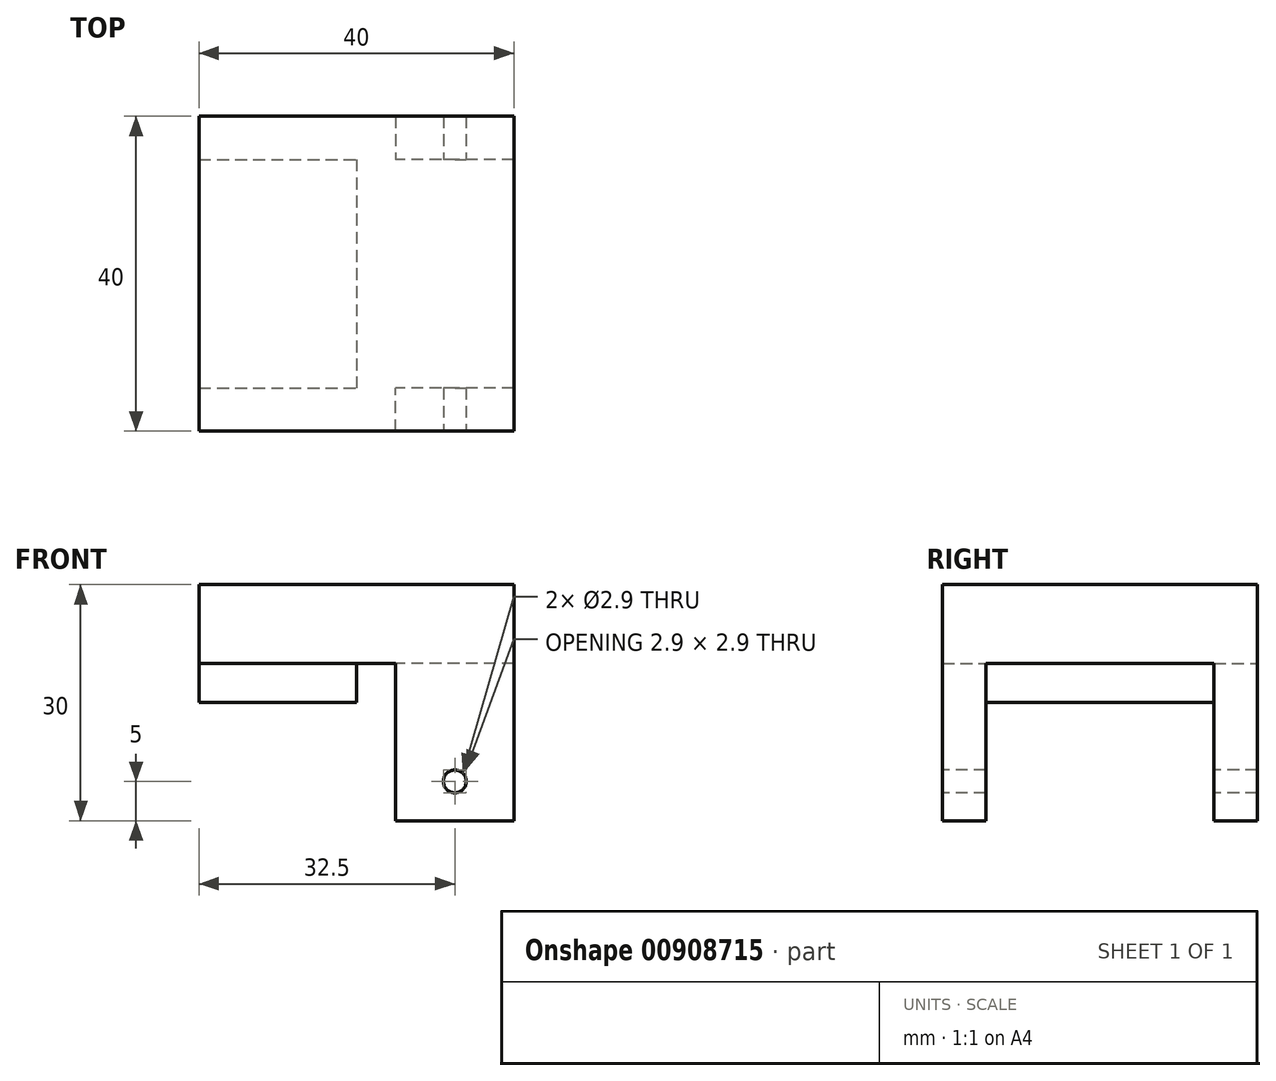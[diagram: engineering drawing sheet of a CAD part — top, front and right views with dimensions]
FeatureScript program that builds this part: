
annotation { "Feature Type Name" : "Feature", "Feature Type Description" : "" }
export const myFeature = defineFeature(function(context is Context, id is Id, definition is map)
    precondition{}
    {
        {
            var Q0;
            Q0=qCreatedBy(makeId("Top.planeOp"),FACE);
            var sketch = newSketch(context, id + "F0", { "sketchPlane" : qUnion([Q0])});
            skLineSegment(sketch, "E0.bottom", {"start": v(20, -20) * mm, "end": v(-20, -20) * mm});
            skLineSegment(sketch, "E0.top", {"start": v(20, 20) * mm, "end": v(-20, 20) * mm});
            skLineSegment(sketch, "E0.left", {"start": v(20, -20) * mm, "end": v(20, 20) * mm});
            skLineSegment(sketch, "E0.right", {"start": v(-20, -20) * mm, "end": v(-20, 20) * mm});
            skPoint(sketch, "E0.middle", {"position": v(0, 0) * mm});
            skSolve(sketch);
        }
        {
            var Q0;
            Q0=makeQuery(id+"F0.imprint","IMPRINT",FACE,{"disambiguationData":[TD([[makeQuery(id+"F0.imprint","IMPRINT",EDGE,{"derivedFrom":sQuery(id+"F0.wireOp",EDGE,"E0.bottom")}),-1.0]])]});
            extrude(context, id + "F1", {"entities" : qUnion([Q0]), "depth" : 10 * mm, "offsetDistance" : 25 * mm});
        }
        {
            var Q0;
            Q0=makeQuery(id+"F1.opExtrude","CAP_FACE",FACE,{"disambiguationData":[OSD([sQuery(id+"F0.wireOp",EDGE,"E0.bottom"),sQuery(id+"F0.wireOp",EDGE,"E0.top"),sQuery(id+"F0.wireOp",EDGE,"E0.left"),sQuery(id+"F0.wireOp",EDGE,"E0.right")])],"isStart":true});
            var sketch = newSketch(context, id + "F2", { "sketchPlane" : qUnion([Q0])});
            skLineSegment(sketch, "E1.bottom", {"start": v(-20, -14.5) * mm, "end": v(0, -14.5) * mm});
            skLineSegment(sketch, "E1.top", {"start": v(-20, 14.5) * mm, "end": v(0, 14.5) * mm});
            skLineSegment(sketch, "E1.left", {"start": v(-20, -14.5) * mm, "end": v(-20, 14.5) * mm});
            skLineSegment(sketch, "E1.right", {"start": v(0, -14.5) * mm, "end": v(0, 14.5) * mm});
            skSolve(sketch);
        }
        {
            var Q0;
            Q0=makeQuery(id+"F2.imprint","IMPRINT",FACE,{"disambiguationData":[TD([[makeQuery(id+"F2.imprint","IMPRINT",EDGE,{"derivedFrom":sQuery(id+"F2.wireOp",EDGE,"E1.bottom")}),1.0]])]});
            extrude(context, id + "F3", {"entities" : qUnion([Q0]), "operationType" : NewBodyOperationType.ADD, "depth" : 5 * mm, "offsetDistance" : 25 * mm});
        }
        {
            var Q0;
            Q0=makeQuery(id+"F1.opExtrude","CAP_FACE",FACE,{"disambiguationData":[OSD([sQuery(id+"F0.wireOp",EDGE,"E0.bottom"),sQuery(id+"F0.wireOp",EDGE,"E0.top"),sQuery(id+"F0.wireOp",EDGE,"E0.left"),sQuery(id+"F0.wireOp",EDGE,"E0.right")])],"isStart":true});
            var sketch = newSketch(context, id + "F4", { "sketchPlane" : qUnion([Q0])});
            skLineSegment(sketch, "E2.bottom", {"start": v(20, 20) * mm, "end": v(5, 20) * mm});
            skLineSegment(sketch, "E2.top", {"start": v(20, 14.5) * mm, "end": v(5, 14.5) * mm});
            skLineSegment(sketch, "E2.left", {"start": v(20, 20) * mm, "end": v(20, 14.5) * mm});
            skLineSegment(sketch, "E2.right", {"start": v(5, 20) * mm, "end": v(5, 14.5) * mm});
            skLineSegment(sketch, "E3.bottom", {"start": v(20, -20) * mm, "end": v(5, -20) * mm});
            skLineSegment(sketch, "E3.top", {"start": v(20, -14.5) * mm, "end": v(5, -14.5) * mm});
            skLineSegment(sketch, "E3.left", {"start": v(20, -20) * mm, "end": v(20, -14.5) * mm});
            skLineSegment(sketch, "E3.right", {"start": v(5, -20) * mm, "end": v(5, -14.5) * mm});
            skSolve(sketch);
        }
        {
            var Q0;
            Q0=makeQuery(id+"F4.imprint","IMPRINT",FACE,{"disambiguationData":[TD([[makeQuery(id+"F4.imprint","IMPRINT",EDGE,{"derivedFrom":sQuery(id+"F4.wireOp",EDGE,"f1VrWO3J-vSY3-jro8-bQ0T-jen6n7x72WjQ.bottom")}),1.0]])]});
            var Q1;
            Q1=makeQuery(id+"F4.imprint","IMPRINT",FACE,{"disambiguationData":[TD([[makeQuery(id+"F4.imprint","IMPRINT",EDGE,{"derivedFrom":sQuery(id+"F4.wireOp",EDGE,"hxVAKMcA-pLjx-TPLh-AbCJ-cGopowbzSFwm.bottom")}),-1.0]])]});
            var Q2;
            Q2=makeQuery(id+"F4.imprint","IMPRINT",FACE,{"disambiguationData":[TD([[makeQuery(id+"F4.imprint","IMPRINT",EDGE,{"derivedFrom":sQuery(id+"F4.wireOp",EDGE,"E2.bottom")}),1.0]])]});
            var Q3;
            Q3=makeQuery(id+"F4.imprint","IMPRINT",FACE,{"disambiguationData":[TD([[makeQuery(id+"F4.imprint","IMPRINT",EDGE,{"derivedFrom":sQuery(id+"F4.wireOp",EDGE,"E3.bottom")}),-1.0]])]});
            extrude(context, id + "F5", {"entities" : qUnion([Q0, Q1, Q2, Q3]), "operationType" : NewBodyOperationType.ADD, "depth" : 20 * mm, "offsetDistance" : 25 * mm});
        }
        {
            var Q0;
            Q0=makeQuery(id+"F5.boolean.opBoolean","MERGE",FACE,{"derivedFrom":[makeQuery(id+"F1.opExtrude","SWEPT_FACE",FACE,{"disambiguationData":[OSD([sQuery(id+"F0.wireOp",EDGE,"E0.bottom")])]}),makeQuery(id+"F5.opExtrude","SWEPT_FACE",FACE,{"disambiguationData":[OSD([sQuery(id+"F4.wireOp",EDGE,"E2.bottom")])]})]});
            var sketch = newSketch(context, id + "F6", { "sketchPlane" : qUnion([Q0])});
            skCircle(sketch, "E4", {"center": v(12.5, -15) * mm, "radius": 1.45 * mm});
            skSolve(sketch);
        }
        {
            var Q0;
            Q0=makeQuery(id+"F6.imprint","IMPRINT",FACE,{"disambiguationData":[TD([[makeQuery(id+"F6.imprint","IMPRINT",EDGE,{"derivedFrom":sQuery(id+"F6.wireOp",EDGE,"E4")}),1.0]])]});
            extrude(context, id + "F7", {"entities" : qUnion([Q0]), "operationType" : NewBodyOperationType.REMOVE, "oppositeDirection" : true, "depth" : 53.2 * mm, "offsetDistance" : 25 * mm});
        }
    });
